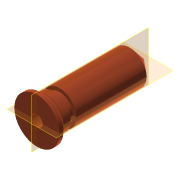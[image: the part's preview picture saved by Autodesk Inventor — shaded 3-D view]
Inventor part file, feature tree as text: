
AUTODESK INVENTOR PART (.ipt)
format: ipt  version: 2016 (Build 200138000, 138)  size: 173,056 bytes
history: native  units: mm
features: sketch x6, extrude x3, revolve x3, chamfer x1
ambient origin geometry x8: Origin, YZ Plane, XZ Plane, XY Plane, X Axis, Y Axis, Z Axis, Center Point
bodies: Solid1 (feature_tree)
feature tree (13):
  extrude  "Extrusion1"  Depth=1.0mm TaperAngle=0.0deg
  extrude  "Extrusion2"  Depth=15.437mm TaperAngle=0.0deg
  extrude  "Extrusion3"  Depth=2.0mm TaperAngle=0.0deg
  revolve  "Revolution1"  [1 undecoded]
  revolve  "Revolution2"  Angle=90.0deg
  chamfer  "Chamfer1"  Angle=90.0deg  [1 undecoded]
  revolve  "Revolution3"  Angle=45.0deg
  sketch  "Sketch1"  dims[d0=8.0mm d1=1.0mm d2=0.0mm]
  sketch  "Sketch2"  dims[d3=6.0mm d4=15.437mm d5=0.0mm]
  sketch  "Sketch3"  dims[d6=2.0mm d7=21.0mm d8=0.0mm]
  sketch  "Sketch4"  dims[d9=6.981317mm d10=0.2mm]
  sketch  "Sketch5"  dims[d11=30.0deg d13=90.0deg]
  sketch  "Sketch6"  dims[d14=0.7mm d15=90.0deg d16=0.3mm d17=2.0mm d18=45.0deg d19=45.0deg d21=0.125mm d22=0.05mm d23=1.0mm d24=0.6mm d25=3.0mm d26=90.0deg]
note: 2 required parameter values undecoded (feature->parameter linkage not recoverable at this tier; creation-order binding heuristic only, values carry confidence <= 0.55)